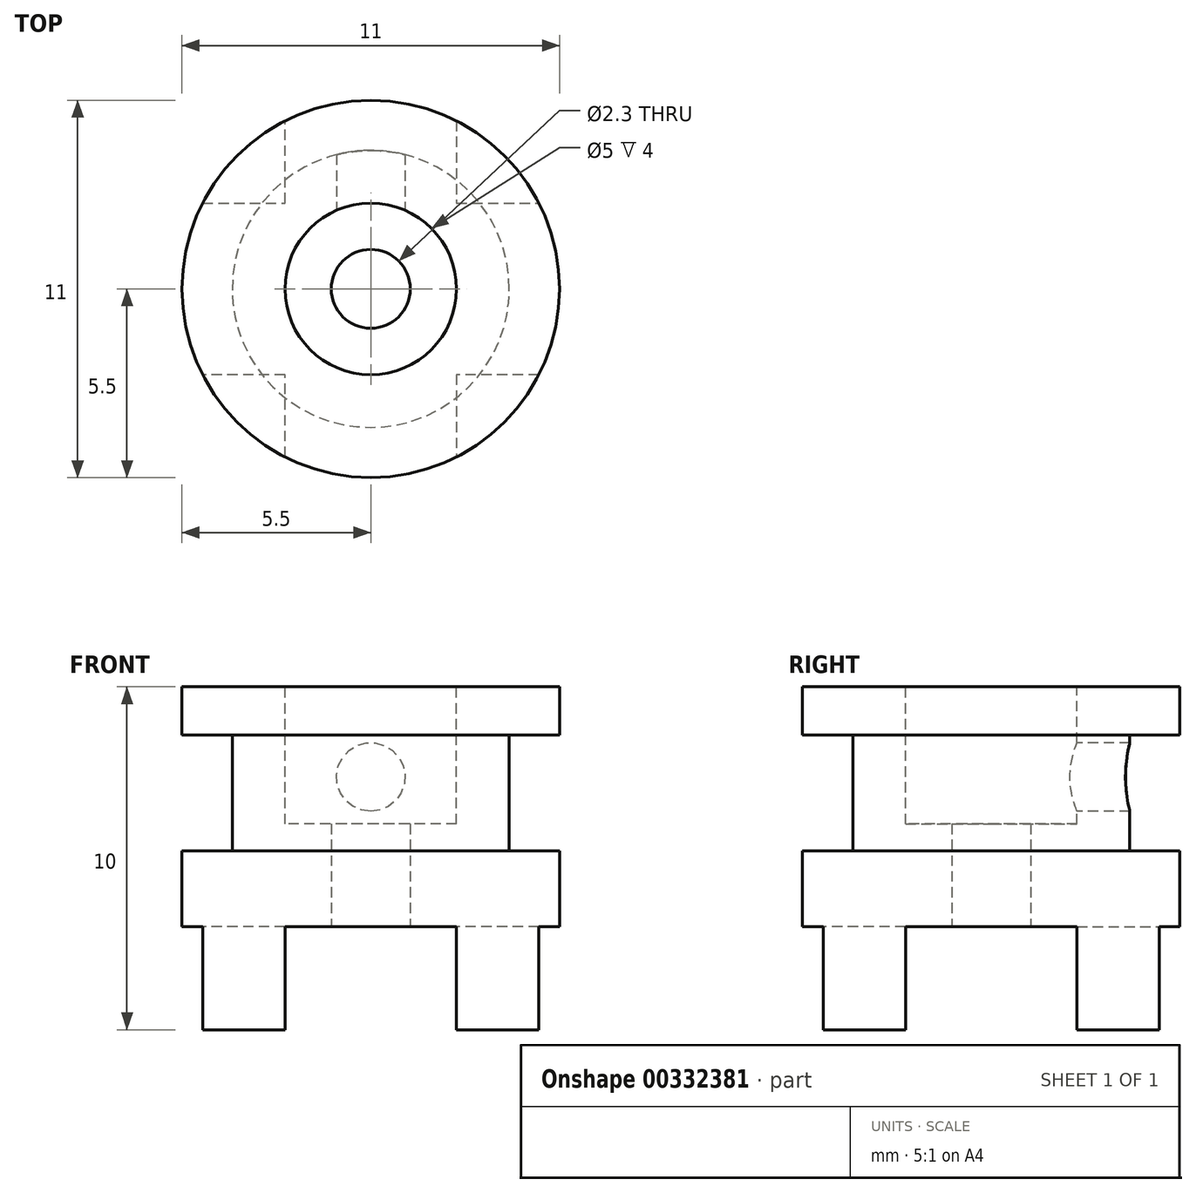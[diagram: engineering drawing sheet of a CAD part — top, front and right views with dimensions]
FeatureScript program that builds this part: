
annotation { "Feature Type Name" : "Feature", "Feature Type Description" : "" }
export const myFeature = defineFeature(function(context is Context, id is Id, definition is map)
    precondition{}
    {
        {
            var Q0;
            Q0=qCreatedBy(makeId("Top.planeOp"),FACE);
            var sketch = newSketch(context, id + "F0", { "sketchPlane" : qUnion([Q0])});
            skCircle(sketch, "E0", {"center": v(0, 0) * mm, "radius": 5.5 * mm});
            skCircle(sketch, "E1", {"center": v(0, 0) * mm, "radius": 1.15 * mm});
            skSolve(sketch);
        }
        {
            var Q0;
            Q0=makeQuery(id+"F0.imprint","IMPRINT",FACE,{"disambiguationData":[TD([[makeQuery(id+"F0.imprint","IMPRINT",EDGE,{"derivedFrom":sQuery(id+"F0.wireOp",EDGE,"E0")}),1.0]])]});
            extrude(context, id + "F1", {"entities" : qUnion([Q0]), "depth" : 7 * mm});
        }
        {
            var Q0;
            Q0=makeQuery(id+"F1.opExtrude","CAP_FACE",FACE,{"disambiguationData":[OSD([sQuery(id+"F0.wireOp",EDGE,"E0")])],"isStart":false});
            var sketch = newSketch(context, id + "F2", { "sketchPlane" : qUnion([Q0])});
            skCircle(sketch, "E2", {"center": v(0, 0) * mm, "radius": 2.5 * mm});
            skSolve(sketch);
        }
        {
            var Q0;
            Q0 = qSketchRegion(id + "F2", true);
            extrude(context, id + "F3", {"entities" : qUnion([Q0]), "operationType" : NewBodyOperationType.REMOVE, "oppositeDirection" : true, "depth" : 4 * mm});
        }
        {
            var Q0;
            Q0=makeQuery(id+"F1.opExtrude","CAP_FACE",FACE,{"disambiguationData":[OSD([sQuery(id+"F0.wireOp",EDGE,"E0"),sQuery(id+"F0.wireOp",EDGE,"E1")])],"isStart":true});
            var sketch = newSketch(context, id + "F4", { "sketchPlane" : qUnion([Q0])});
            skLineSegment(sketch, "E3", {"start": v(-2.5, 4.9) * mm, "end": v(-2.5, 2.5) * mm});
            skLineSegment(sketch, "E4", {"start": v(-2.5, 2.5) * mm, "end": v(-4.9, 2.5) * mm});
            skArc(sketch, "E5", {"start": v(-2.5, 4.9) * mm, "mid": v(-3.89, 3.89) * mm, "end": v(-4.9, 2.5) * mm});
            skArc(sketch, "E6.1.0", {"start": v(-4.9, -2.5) * mm, "mid": v(-3.89, -3.89) * mm, "end": v(-2.5, -4.9) * mm});
            skLineSegment(sketch, "E6.1.1", {"start": v(-2.5, -2.5) * mm, "end": v(-2.5, -4.9) * mm});
            skLineSegment(sketch, "E6.1.2", {"start": v(-4.9, -2.5) * mm, "end": v(-2.5, -2.5) * mm});
            skArc(sketch, "E6.2.0", {"start": v(2.5, -4.9) * mm, "mid": v(3.89, -3.89) * mm, "end": v(4.9, -2.5) * mm});
            skLineSegment(sketch, "E6.2.1", {"start": v(2.5, -2.5) * mm, "end": v(4.9, -2.5) * mm});
            skLineSegment(sketch, "E6.2.2", {"start": v(2.5, -4.9) * mm, "end": v(2.5, -2.5) * mm});
            skArc(sketch, "E6.3.0", {"start": v(4.9, 2.5) * mm, "mid": v(3.89, 3.89) * mm, "end": v(2.5, 4.9) * mm});
            skLineSegment(sketch, "E6.3.1", {"start": v(2.5, 2.5) * mm, "end": v(2.5, 4.9) * mm});
            skLineSegment(sketch, "E6.3.2", {"start": v(4.9, 2.5) * mm, "end": v(2.5, 2.5) * mm});
            skSolve(sketch);
        }
        {
            var Q0;
            Q0 = qSketchRegion(id + "F4", true);
            extrude(context, id + "F5", {"entities" : qUnion([Q0]), "operationType" : NewBodyOperationType.ADD, "depth" : 3 * mm});
        }
        {
            var Q0;
            Q0=qCreatedBy(makeId("Front.planeOp"),FACE);
            var sketch = newSketch(context, id + "F6", { "sketchPlane" : qUnion([Q0])});
            skLineSegment(sketch, "E7.bottom", {"start": v(-6.35, 5.6) * mm, "end": v(-4.04, 5.6) * mm});
            skLineSegment(sketch, "E7.top", {"start": v(-6.35, 2.22) * mm, "end": v(-4.04, 2.22) * mm});
            skLineSegment(sketch, "E7.left", {"start": v(-6.35, 5.6) * mm, "end": v(-6.35, 2.22) * mm});
            skLineSegment(sketch, "E7.right", {"start": v(-4.04, 5.6) * mm, "end": v(-4.04, 2.22) * mm});
            skSolve(sketch);
        }
        {
            var Q0;
            Q0 = qSketchRegion(id + "F6", true);
            var Q1;
            Q1=makeQuery(id+"F3.boolean.opBoolean","COPY",FACE,{"derivedFrom":makeQuery(id+"F3.opExtrude","SWEPT_FACE",FACE,{"disambiguationData":[OSD([sQuery(id+"F2.wireOp",EDGE,"E2")])]})});
            revolve(context, id + "F7", {"operationType" : NewBodyOperationType.REMOVE, "entities" : qUnion([Q0]), "axis" : qUnion([Q1]), "revolveType" : RevolveType.FULL, "oppositeDirection" : true});
        }
        {
            var Q0;
            Q0=qCreatedBy(makeId("Front.planeOp"),FACE);
            var sketch = newSketch(context, id + "F8", { "sketchPlane" : qUnion([Q0])});
            skCircle(sketch, "E8", {"center": v(0, 4.37) * mm, "radius": 1 * mm});
            skSolve(sketch);
        }
        {
            var Q0;
            Q0 = qSketchRegion(id + "F8", true);
            extrude(context, id + "F9", {"entities" : qUnion([Q0]), "operationType" : NewBodyOperationType.REMOVE, "oppositeDirection" : true, "depth" : 25 * mm});
        }
    });
